# Revit family: SKSMUKabelrinne SKS-Magic® 85 ungelocht FS_FT_830_840_850_860
name_source: partatom
category: Generic Models
revit_build: Autodesk Revit 2017 (Build: 20190508_0315(x64)
units: mm (PartAtom-declared; Revit-internal decimal feet)

## family parameters
Always vertical = Yes
Can host rebar = No
Cut with Voids When Loaded = No
Part Type = Normal
Room Calculation Point = No
Round Connector Dimension = Use Diameter
Shared = No
Work Plane-Based = No

## types (8) — shared parameters
Cut's number = 2
Height = 85 mm  [stored 0.278871 ft]
Length = 3050 mm  [stored 10.0066 ft]
Length 1 = 3000 mm  [stored 9.84252 ft]
Length 2 = 50 mm  [stored 0.164042 ft]
Manufacturer = OBO BETTERMANN
URL = http://www.obo-bettermann.com
Width 2 = 7 mm  [stored 0.0229659 ft]

## per-type parameters (varying)
| type | GTIN | Manufacturer Art.No. | Material | Width | Width 1 |
| SKSMU 830 FS | 4012195833505 | 6059768 | Strip-galvanised | 300 mm | 150 mm |
| SKSMU 830 FT | 4012195833628 | 6059785 | Hot dip galvanised | 300 mm | 150 mm |
| SKSMU 840 FS | 4012195833512 | 6059770 | Strip-galvanised | 400 mm  [stored 1.31234 ft] | 200 mm  [stored 0.656168 ft] |
| SKSMU 840 FT | 4012195833635 | 6059787 | Hot dip galvanised | 400 mm  [stored 1.31234 ft] | 200 mm  [stored 0.656168 ft] |
| SKSMU 850 FS | 4012195833529 | 6059772 | Strip-galvanised | 500 mm  [stored 1.64042 ft] | 250 mm  [stored 0.82021 ft] |
| SKSMU 850 FT | 4012195833642 | 6059789 | Hot dip galvanised | 500 mm  [stored 1.64042 ft] | 250 mm  [stored 0.82021 ft] |
| SKSMU 860 FS | 4012195833550 | 6059774 | Strip-galvanised | 600 mm | 300 mm |
| SKSMU 860 FT | 4012195833673 | 6059791 | Hot dip galvanised | 600 mm | 300 mm |

note: column(s) folded — value = type name in every type: Article Type

note: [stored X ft] marks values corroborated as IEEE doubles in the binary element streams (Revit-internal decimal feet)

## geometry (parser evidence)
native form markers: Sweep x1
no freeform markers — native parametric forms only
